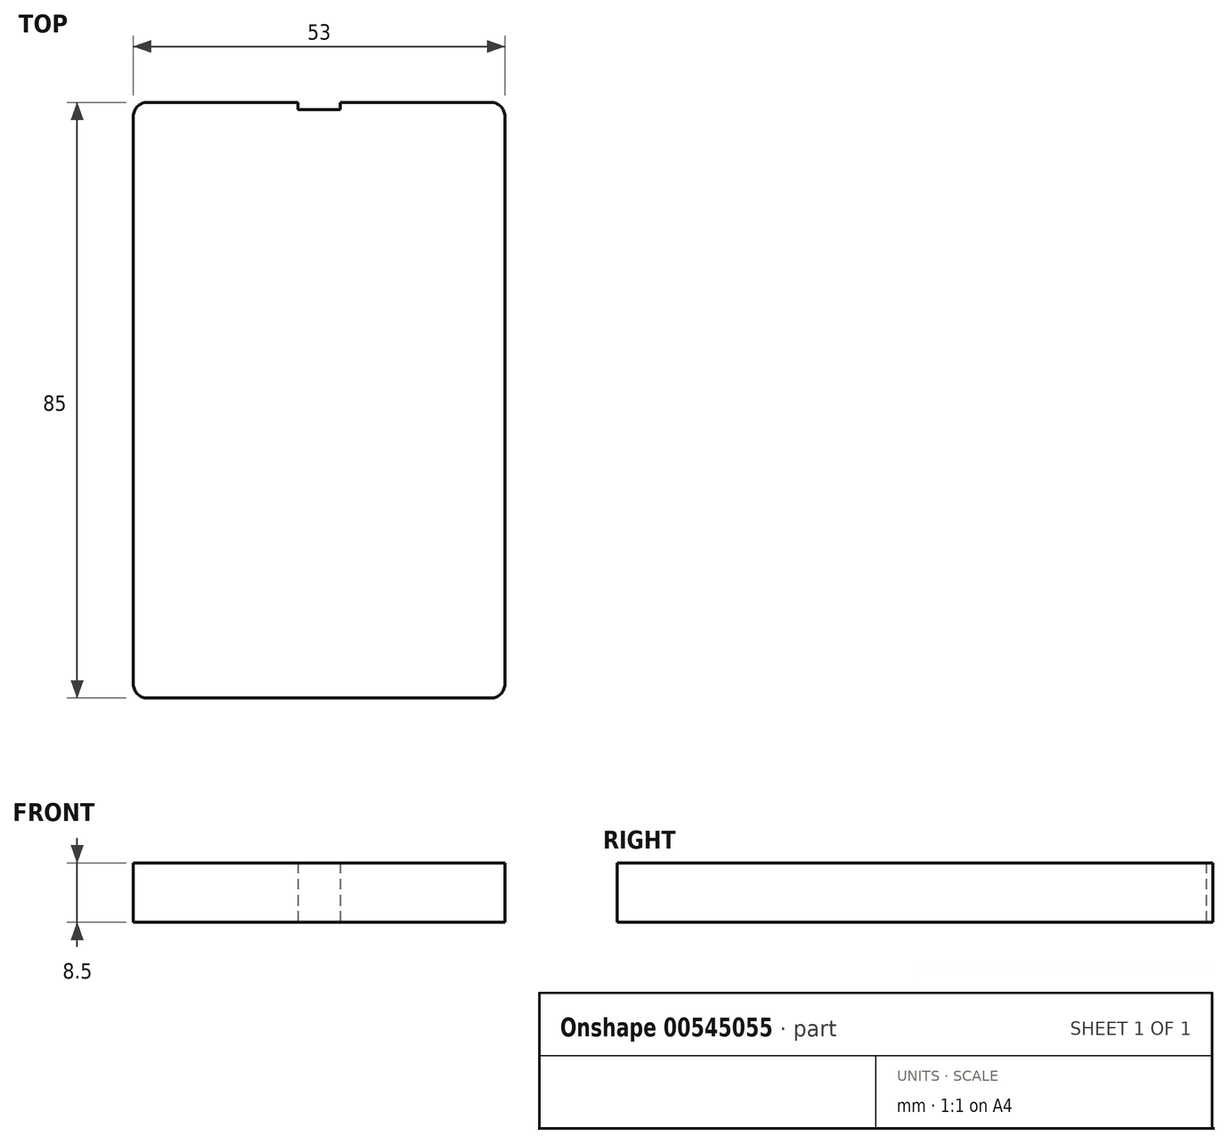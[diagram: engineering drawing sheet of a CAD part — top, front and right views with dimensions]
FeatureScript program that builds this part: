
annotation { "Feature Type Name" : "Feature", "Feature Type Description" : "" }
export const myFeature = defineFeature(function(context is Context, id is Id, definition is map)
    precondition{}
    {
        {
            var Q0;
            Q0=qCreatedBy(makeId("Top.planeOp"),FACE);
            var sketch = newSketch(context, id + "F0", { "sketchPlane" : qUnion([Q0])});
            skLineSegment(sketch, "E0.bottom", {"start": v(26.5, -42.5) * mm, "end": v(-26.5, -42.5) * mm});
            skLineSegment(sketch, "E0.top", {"start": v(26.5, 42.5) * mm, "end": v(3, 42.5) * mm});
            skLineSegment(sketch, "E0.left", {"start": v(26.5, -42.5) * mm, "end": v(26.5, 42.5) * mm});
            skLineSegment(sketch, "E0.right", {"start": v(-26.5, -42.5) * mm, "end": v(-26.5, 42.5) * mm});
            skPoint(sketch, "E0.middle", {"position": v(0, 0) * mm});
            skLineSegment(sketch, "E1.bottom", {"start": v(3, 41.5) * mm, "end": v(-3, 41.5) * mm});
            skLineSegment(sketch, "E1.left", {"start": v(3, 41.5) * mm, "end": v(3, 42.5) * mm});
            skLineSegment(sketch, "E1.right", {"start": v(-3, 41.5) * mm, "end": v(-3, 42.5) * mm});
            skPoint(sketch, "E1.middle", {"position": v(0, 42.5) * mm});
            skLineSegment(sketch, "E2.trimOffspring", {"start": v(-3, 42.5) * mm, "end": v(-26.5, 42.5) * mm});
            skSolve(sketch);
        }
        {
            var Q0;
            Q0=makeQuery(id+"F0.imprint","IMPRINT",FACE,{"disambiguationData":[TD([[makeQuery(id+"F0.imprint","IMPRINT",EDGE,{"derivedFrom":sQuery(id+"F0.wireOp",EDGE,"E0.bottom")}),-1.0]])]});
            extrude(context, id + "F1", {"entities" : qUnion([Q0]), "endBound" : BoundingType.SYMMETRIC, "depth" : 8.5 * mm, "offsetDistance" : 25 * mm});
        }
        {
            var Q0;
            Q0=makeQuery(id+"F1.opExtrude","SWEPT_EDGE",EDGE,{"disambiguationData":[OSD([sQuery(id+"F0.wireOp",EDGE,"E0.bottom"),sQuery(id+"F0.wireOp",EDGE,"E0.right")])]});
            var Q1;
            Q1=makeQuery(id+"F1.opExtrude","SWEPT_EDGE",EDGE,{"disambiguationData":[OSD([sQuery(id+"F0.wireOp",EDGE,"E0.bottom"),sQuery(id+"F0.wireOp",EDGE,"E0.left")])]});
            var Q2;
            Q2=makeQuery(id+"F1.opExtrude","SWEPT_EDGE",EDGE,{"disambiguationData":[OSD([sQuery(id+"F0.wireOp",EDGE,"E0.top"),sQuery(id+"F0.wireOp",EDGE,"E0.left")])]});
            var Q3;
            Q3=makeQuery(id+"F1.opExtrude","SWEPT_EDGE",EDGE,{"disambiguationData":[OSD([sQuery(id+"F0.wireOp",EDGE,"E0.right"),sQuery(id+"F0.wireOp",EDGE,"E2.trimOffspring")])]});
            fillet(context, id + "F2", {"entities" : qUnion([Q0, Q1, Q2, Q3]), "radius" : 2 * mm, "tangentPropagation" : true, "allowEdgeOverflow" : false});
        }
    });
